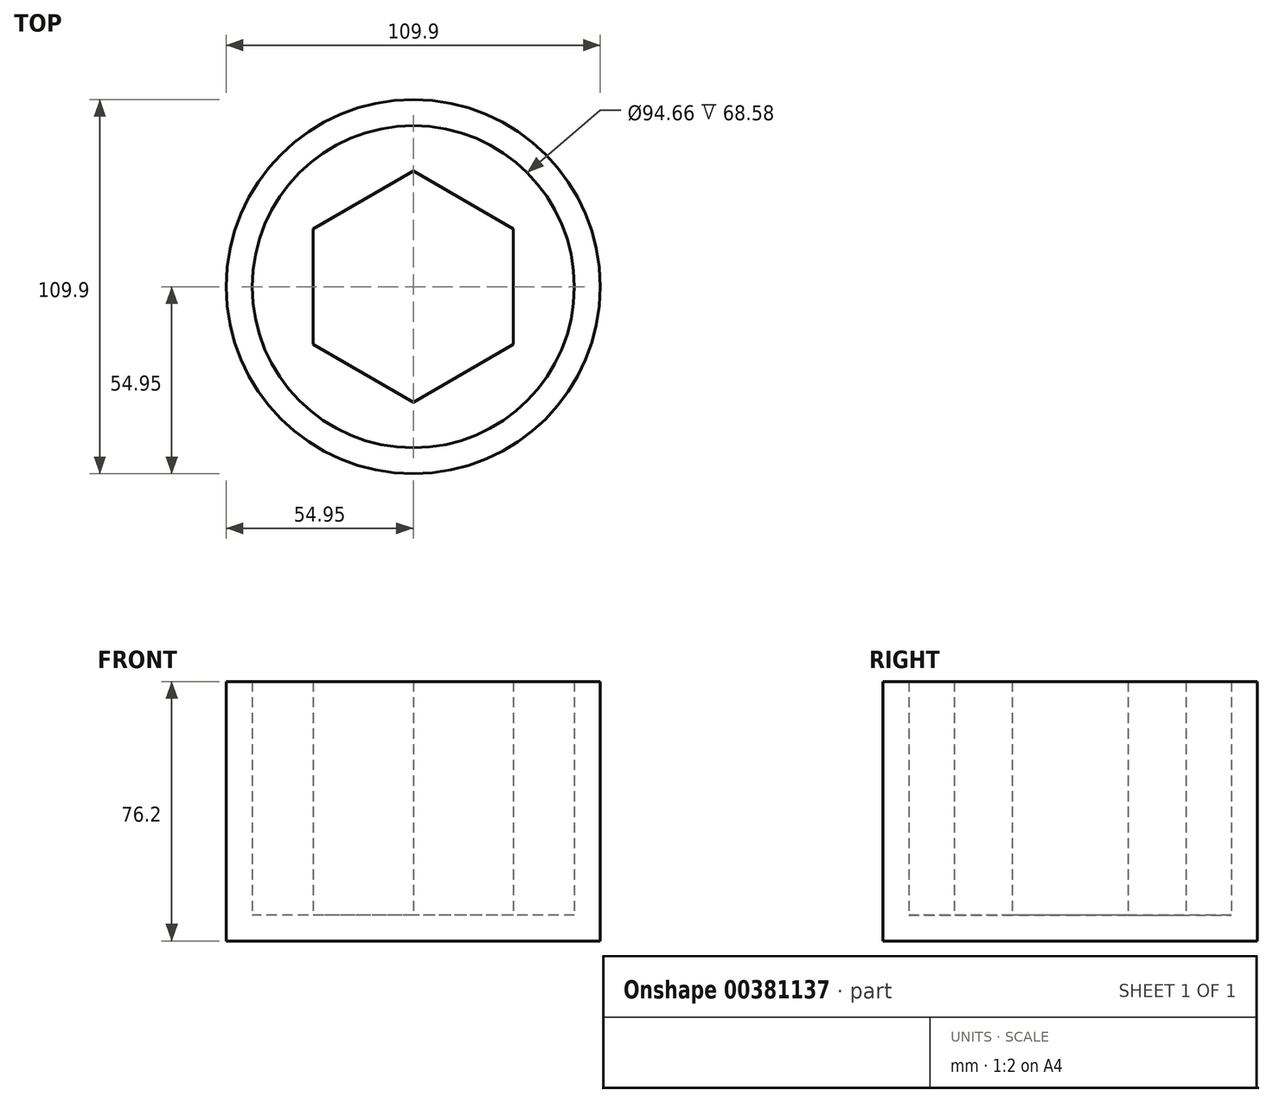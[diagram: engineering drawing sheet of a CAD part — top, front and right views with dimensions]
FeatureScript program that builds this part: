
annotation { "Feature Type Name" : "Feature", "Feature Type Description" : "" }
export const myFeature = defineFeature(function(context is Context, id is Id, definition is map)
    precondition{}
    {
        {
            var Q0;
            Q0=qCreatedBy(makeId("Top.planeOp"),FACE);
            var sketch = newSketch(context, id + "F0", { "sketchPlane" : qUnion([Q0])});
            skCircle(sketch, "E0", {"center": v(0, 0) * mm, "radius": 54.95 * mm});
            skSolve(sketch);
        }
        {
            var Q0;
            Q0=qSketchRegion(id+"F0",true);
            extrude(context, id + "F1", {"entities" : qUnion([Q0]), "depth" : 50.8 * mm, "hasSecondDirection" : true, "secondDirectionOppositeDirection" : true, "secondDirectionDepth" : 25.4 * mm});
        }
        {
            var Q0;
            Q0=makeQuery(id+"F1.opExtrude","CAP_FACE",FACE,{"disambiguationData":[OSD([sQuery(id+"F0.wireOp",EDGE,"E0")])],"isStart":false});
            shell(context, id + "F2", {"entities" : qUnion([Q0]), "thickness" : 7.62 * mm});
        }
        {
            var Q0;
            {var subQ0=sQuery(id+"F0.wireOp",EDGE,"E0");Q0=makeQuery(id+"F2.opShell","OFFSET_FACE",FACE,{"disambiguationData":[OSD([subQ0]),TDD([makeQuery(id+"F1.opExtrude","CAP_FACE",FACE,{"disambiguationData":[OSD([subQ0])],"isStart":true})])]});}
            var sketch = newSketch(context, id + "F3", { "sketchPlane" : qUnion([Q0])});
            skCircle(sketch, "E1.cCircle", {"center": v(0, 0) * mm, "radius": 29.44 * mm, "construction": true});
            skLineSegment(sketch, "E1.0", {"start": v(29.44, 17) * mm, "end": v(29.44, -17) * mm});
            skLineSegment(sketch, "E1.1", {"start": v(29.44, -17) * mm, "end": v(0, -34) * mm});
            skLineSegment(sketch, "E1.2", {"start": v(0, -34) * mm, "end": v(-29.44, -17) * mm});
            skLineSegment(sketch, "E1.3", {"start": v(-29.44, -17) * mm, "end": v(-29.44, 17) * mm});
            skLineSegment(sketch, "E1.4", {"start": v(-29.44, 17) * mm, "end": v(0, 34) * mm});
            skLineSegment(sketch, "E1.5", {"start": v(0, 34) * mm, "end": v(29.44, 17) * mm});
            skPoint(sketch, "E1.0.midPoint", {"position": v(29.44, 0) * mm});
            skSolve(sketch);
        }
        {
            var Q0;
            Q0=qSketchRegion(id+"F3",true);
            extrude(context, id + "F4", {"entities" : qUnion([Q0]), "operationType" : NewBodyOperationType.ADD, "depth" : 68.58 * mm});
        }
    });
